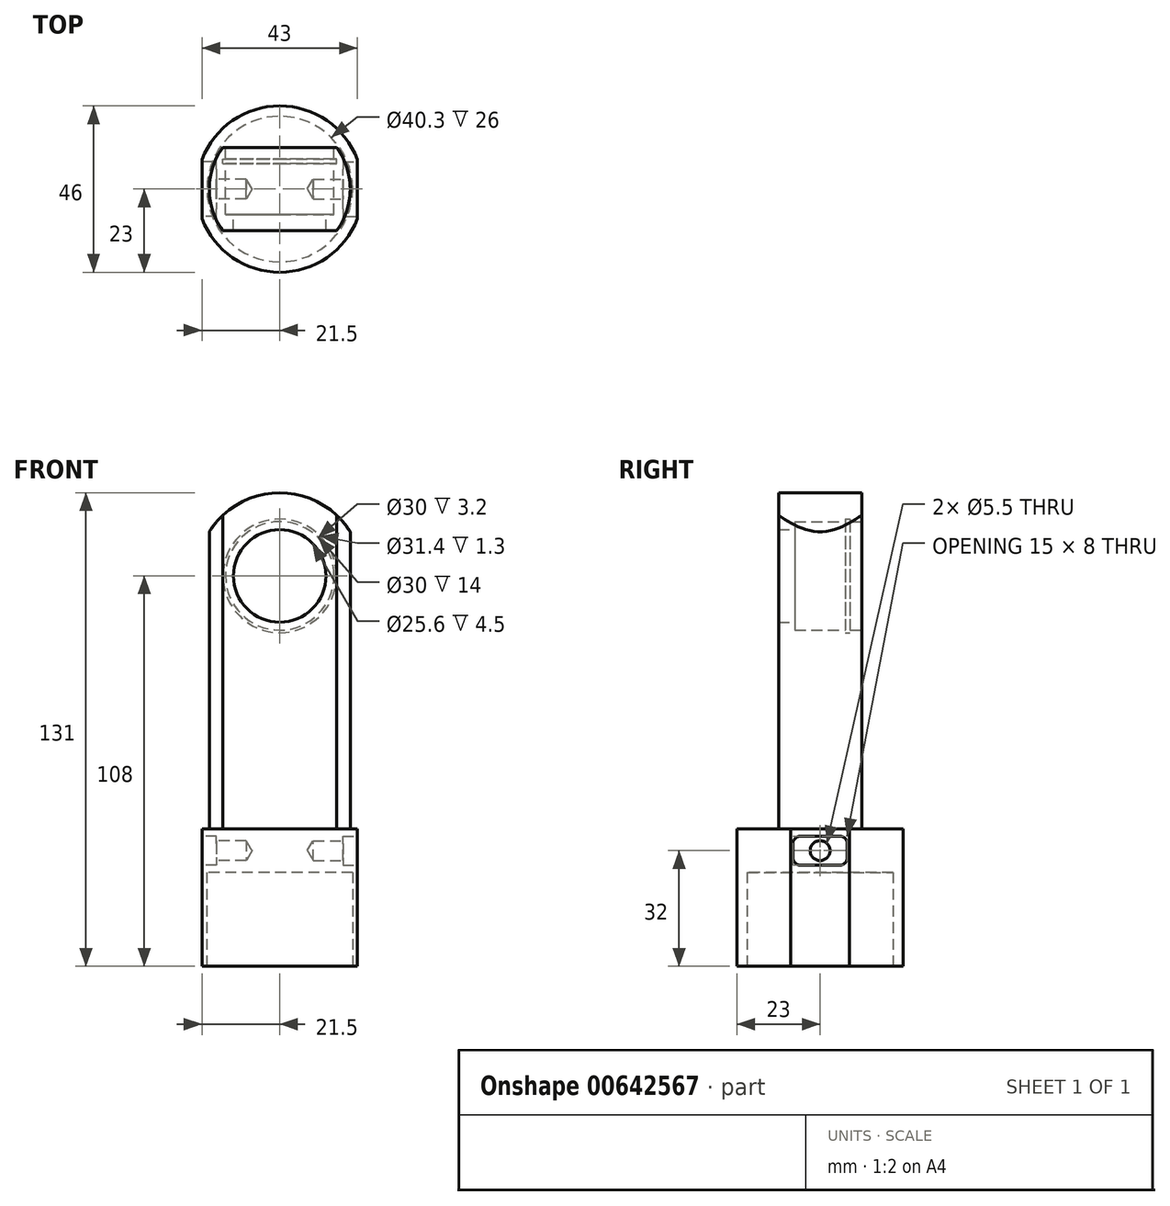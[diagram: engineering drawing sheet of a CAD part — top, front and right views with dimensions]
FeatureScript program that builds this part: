
annotation { "Feature Type Name" : "Feature", "Feature Type Description" : "" }
export const myFeature = defineFeature(function(context is Context, id is Id, definition is map)
    precondition{}
    {
        {
            var Q0;
            Q0=qCreatedBy(makeId("Top.planeOp"),FACE);
            var sketch = newSketch(context, id + "F0", { "sketchPlane" : qUnion([Q0])});
            skArc(sketch, "E0", {"start": v(-8.17, 21.5) * mm, "mid": v(-16.26, 16.26) * mm, "end": v(-21.5, 8.17) * mm});
            skArc(sketch, "E1.trimOffspring", {"start": v(8.17, -21.5) * mm, "mid": v(16.26, -16.26) * mm, "end": v(21.5, -8.17) * mm});
            skArc(sketch, "E2", {"start": v(-21.5, -8.17) * mm, "mid": v(0, -23) * mm, "end": v(21.5, -8.17) * mm});
            skLineSegment(sketch, "E3", {"start": v(-21.5, -8.17) * mm, "end": v(-21.5, 8.17) * mm});
            skLineSegment(sketch, "E4.MirrorCS", {"start": v(21.5, -8.17) * mm, "end": v(21.5, 8.17) * mm});
            skArc(sketch, "E5.trimOffspring", {"start": v(-21.5, -8.17) * mm, "mid": v(-16.26, -16.26) * mm, "end": v(-8.17, -21.5) * mm});
            skArc(sketch, "E6.trimOffspring", {"start": v(21.5, 8.17) * mm, "mid": v(0, 23) * mm, "end": v(-21.5, 8.17) * mm});
            skArc(sketch, "E7.trimOffspring", {"start": v(21.5, 8.17) * mm, "mid": v(16.26, 16.26) * mm, "end": v(8.17, 21.5) * mm});
            skSolve(sketch);
        }
        {
            var Q0;
            {var subQ2=sQuery(id+"F0.wireOp",EDGE,"E3");Q0=makeQuery(id+"F0.imprint","IMPRINT",FACE,{"disambiguationData":[TD([[makeQuery(id+"F0.imprint","IMPRINT",EDGE,{"derivedFrom":subQ2}),-1.0]])]});}
            extrude(context, id + "F1", {"entities" : qUnion([Q0]), "depth" : 38 * mm, "offsetDistance" : 25 * mm});
        }
        {
            var Q0;
            Q0=qCreatedBy(makeId("Top.planeOp"),FACE);
            var sketch = newSketch(context, id + "F2", { "sketchPlane" : qUnion([Q0])});
            skCircle(sketch, "E8", {"center": v(0, 0) * mm, "radius": 20.15 * mm});
            skSolve(sketch);
        }
        {
            var Q0;
            Q0=makeQuery(id+"F2.imprint","IMPRINT",FACE,{"disambiguationData":[TD([[makeQuery(id+"F2.imprint","IMPRINT",EDGE,{"derivedFrom":sQuery(id+"F2.wireOp",EDGE,"E8")}),1.0]])]});
            extrude(context, id + "F3", {"entities" : qUnion([Q0]), "operationType" : NewBodyOperationType.REMOVE, "depth" : 26 * mm, "offsetDistance" : 25 * mm});
        }
        {
            var Q0;
            Q0=makeQuery(id+"F1.opExtrude","CAP_FACE",FACE,{"disambiguationData":[OSD([sQuery(id+"F0.wireOp",EDGE,"E2"),sQuery(id+"F0.wireOp",EDGE,"E3"),sQuery(id+"F0.wireOp",EDGE,"E4.MirrorCS"),sQuery(id+"F0.wireOp",EDGE,"E5.trimOffspring"),sQuery(id+"F0.wireOp",EDGE,"E6.trimOffspring"),sQuery(id+"F0.wireOp",EDGE,"E7.trimOffspring")])],"isStart":false});
            var sketch = newSketch(context, id + "F4", { "sketchPlane" : qUnion([Q0])});
            skArc(sketch, "E9", {"start": v(-15.75, 11.5) * mm, "mid": v(-19.5, 0) * mm, "end": v(-15.75, -11.5) * mm});
            skLineSegment(sketch, "E10", {"start": v(-15.75, 11.5) * mm, "end": v(15.75, 11.5) * mm});
            skLineSegment(sketch, "E11.MirrorCS", {"start": v(-15.75, -11.5) * mm, "end": v(15.75, -11.5) * mm});
            skArc(sketch, "E12.trimOffspring", {"start": v(15.75, -11.5) * mm, "mid": v(19.5, 0) * mm, "end": v(15.75, 11.5) * mm});
            skSolve(sketch);
        }
        {
            var Q0;
            Q0=makeQuery(id+"F4.imprint","IMPRINT",FACE,{"disambiguationData":[TD([[makeQuery(id+"F4.imprint","IMPRINT",EDGE,{"derivedFrom":sQuery(id+"F4.wireOp",EDGE,"E9")}),1.0]])]});
            extrude(context, id + "F5", {"entities" : qUnion([Q0]), "operationType" : NewBodyOperationType.ADD, "depth" : 93 * mm, "offsetDistance" : 25 * mm});
        }
        {
            var Q0;
            Q0=qCreatedBy(makeId("Front.planeOp"),FACE);
            var sketch = newSketch(context, id + "F6", { "sketchPlane" : qUnion([Q0])});
            skArc(sketch, "E13", {"start": v(22.8, 111.07) * mm, "mid": v(-1.45, 130.95) * mm, "end": v(-23, 108.17) * mm});
            skLineSegment(sketch, "E14", {"start": v(-23, 108.17) * mm, "end": v(-36.61, 135.54) * mm});
            skLineSegment(sketch, "E15", {"start": v(-36.61, 135.54) * mm, "end": v(28.1, 135.54) * mm});
            skLineSegment(sketch, "E16", {"start": v(28.1, 135.54) * mm, "end": v(22.8, 111.07) * mm});
            skSolve(sketch);
        }
        {
            var Q0;
            Q0 = qSketchRegion(id + "F6", true);
            extrude(context, id + "F7", {"entities" : qUnion([Q0]), "operationType" : NewBodyOperationType.REMOVE, "oppositeDirection" : true, "depth" : 25 * mm, "offsetDistance" : 25 * mm, "symmetric" : true});
        }
        {
            var Q0;
            Q0=makeQuery(id+"F5.opExtrude","SWEPT_FACE",FACE,{"disambiguationData":[OSD([sQuery(id+"F4.wireOp",EDGE,"E10")])]});
            var sketch = newSketch(context, id + "F8", { "sketchPlane" : qUnion([Q0])});
            skCircle(sketch, "E17", {"center": v(0, 108) * mm, "radius": 15 * mm});
            skSolve(sketch);
        }
        {
            var Q0;
            Q0 = qSketchRegion(id + "F8", true);
            extrude(context, id + "F9", {"entities" : qUnion([Q0]), "operationType" : NewBodyOperationType.REMOVE, "oppositeDirection" : true, "depth" : 3.2 * mm, "offsetDistance" : 25 * mm});
        }
        {
            var Q0;
            Q0=makeQuery(id+"F9.boolean.opBoolean","COPY",FACE,{"derivedFrom":makeQuery(id+"F9.opExtrude","CAP_FACE",FACE,{"disambiguationData":[OSD([sQuery(id+"F8.wireOp",EDGE,"E17")])],"isStart":false})});
            var sketch = newSketch(context, id + "F10", { "sketchPlane" : qUnion([Q0])});
            skCircle(sketch, "E18", {"center": v(0, 108) * mm, "radius": 15.7 * mm});
            skSolve(sketch);
        }
        {
            var Q0;
            Q0 = qSketchRegion(id + "F10", true);
            extrude(context, id + "F11", {"entities" : qUnion([Q0]), "operationType" : NewBodyOperationType.REMOVE, "oppositeDirection" : true, "depth" : 1.3 * mm, "offsetDistance" : 25 * mm});
        }
        {
            var Q0;
            Q0=makeQuery(id+"F11.boolean.opBoolean","COPY",FACE,{"derivedFrom":makeQuery(id+"F11.opExtrude","CAP_FACE",FACE,{"disambiguationData":[OSD([sQuery(id+"F10.wireOp",EDGE,"E18")])],"isStart":false})});
            var sketch = newSketch(context, id + "F12", { "sketchPlane" : qUnion([Q0])});
            skCircle(sketch, "E19", {"center": v(0, 108) * mm, "radius": 15 * mm});
            skSolve(sketch);
        }
        {
            var Q0;
            Q0 = qSketchRegion(id + "F12", true);
            extrude(context, id + "F13", {"entities" : qUnion([Q0]), "operationType" : NewBodyOperationType.REMOVE, "oppositeDirection" : true, "depth" : 14 * mm, "offsetDistance" : 25 * mm});
        }
        {
            var Q0;
            Q0=makeQuery(id+"F13.boolean.opBoolean","COPY",FACE,{"derivedFrom":makeQuery(id+"F13.opExtrude","CAP_FACE",FACE,{"disambiguationData":[OSD([sQuery(id+"F12.wireOp",EDGE,"E19")])],"isStart":false})});
            var sketch = newSketch(context, id + "F14", { "sketchPlane" : qUnion([Q0])});
            skCircle(sketch, "E20", {"center": v(0, 108) * mm, "radius": 12.8 * mm});
            skSolve(sketch);
        }
        {
            var Q0;
            Q0 = qSketchRegion(id + "F14", true);
            extrude(context, id + "F15", {"entities" : qUnion([Q0]), "operationType" : NewBodyOperationType.REMOVE, "endBound" : BoundingType.THROUGH_ALL, "oppositeDirection" : true, "depth" : 25 * mm, "offsetDistance" : 25 * mm});
        }
        {
            var Q0;
            Q0=makeQuery(id+"F1.opExtrude","SWEPT_FACE",FACE,{"disambiguationData":[OSD([sQuery(id+"F0.wireOp",EDGE,"E4.MirrorCS")])]});
            var sketch = newSketch(context, id + "F16", { "sketchPlane" : qUnion([Q0])});
            skLineSegment(sketch, "E21.bottom", {"start": v(-5.5, 36) * mm, "end": v(5.5, 36) * mm});
            skLineSegment(sketch, "E21.top", {"start": v(-5.5, 28) * mm, "end": v(5.5, 28) * mm});
            skLineSegment(sketch, "E21.left", {"start": v(-7.5, 34) * mm, "end": v(-7.5, 30) * mm});
            skLineSegment(sketch, "E21.right", {"start": v(7.5, 34) * mm, "end": v(7.5, 30) * mm});
            skPoint(sketch, "E21.middle", {"position": v(0, 32) * mm});
            skPoint(sketch, "E22.visualSharp", {"position": v(-7.5, 36) * mm});
            skArc(sketch, "E22.filletArc", {"start": v(-5.5, 36) * mm, "mid": v(-6.91, 35.41) * mm, "end": v(-7.5, 34) * mm});
            skPoint(sketch, "E23.visualSharp", {"position": v(7.5, 36) * mm});
            skArc(sketch, "E23.filletArc", {"start": v(7.5, 34) * mm, "mid": v(6.91, 35.41) * mm, "end": v(5.5, 36) * mm});
            skPoint(sketch, "E24.visualSharp", {"position": v(7.5, 28) * mm});
            skArc(sketch, "E24.filletArc", {"start": v(5.5, 28) * mm, "mid": v(6.91, 28.59) * mm, "end": v(7.5, 30) * mm});
            skPoint(sketch, "E25.visualSharp", {"position": v(-7.5, 28) * mm});
            skArc(sketch, "E25.filletArc", {"start": v(-7.5, 30) * mm, "mid": v(-6.91, 28.59) * mm, "end": v(-5.5, 28) * mm});
            skSolve(sketch);
        }
        {
            var Q0;
            Q0 = qSketchRegion(id + "F16", true);
            extrude(context, id + "F17", {"entities" : qUnion([Q0]), "operationType" : NewBodyOperationType.REMOVE, "oppositeDirection" : true, "depth" : 4 * mm, "offsetDistance" : 25 * mm});
        }
        {
            var Q0;
            Q0=makeQuery(id+"F17.boolean.opBoolean","COPY",FACE,{"derivedFrom":makeQuery(id+"F17.opExtrude","CAP_FACE",FACE,{"disambiguationData":[OSD([sQuery(id+"F16.wireOp",EDGE,"E21.bottom"),sQuery(id+"F16.wireOp",EDGE,"E21.top"),sQuery(id+"F16.wireOp",EDGE,"E21.left"),sQuery(id+"F16.wireOp",EDGE,"E21.right"),sQuery(id+"F16.wireOp",EDGE,"E22.filletArc"),sQuery(id+"F16.wireOp",EDGE,"E23.filletArc"),sQuery(id+"F16.wireOp",EDGE,"E24.filletArc"),sQuery(id+"F16.wireOp",EDGE,"E25.filletArc")])],"isStart":false})});
            var sketch = newSketch(context, id + "F18", { "sketchPlane" : qUnion([Q0])});
            skPoint(sketch, "E26", {"position": v(0, 32) * mm});
            skSolve(sketch);
        }
        {
            var Q0;
            Q0=sQuery(id+"F18.wireOp",VERTEX,"E26");
            var Q1;
            Q1=makeQuery(id+"F1.opExtrude","SWEPT_BODY",BODY,{"disambiguationData":[OSD([sQuery(id+"F0.wireOp",EDGE,"E2"),sQuery(id+"F0.wireOp",EDGE,"E3"),sQuery(id+"F0.wireOp",EDGE,"E4.MirrorCS"),sQuery(id+"F0.wireOp",EDGE,"E5.trimOffspring"),sQuery(id+"F0.wireOp",EDGE,"E6.trimOffspring"),sQuery(id+"F0.wireOp",EDGE,"E7.trimOffspring")])]});
            hole(context, id + "F19", {"style" : HoleStyle.SIMPLE, "endStyle" : HoleEndStyle.BLIND, "holeDiameter" : 5.5 * mm, "majorDiameter" : 5 * mm, "holeDepth" : 8.2 * mm, "isTappedThrough" : true, "tappedDepth" : 12 * mm, "tapClearance" : 3, "locations" : qUnion([Q0]), "scope" : qUnion([Q1])});
        }
        {
            var Q0;
            Q0=makeQuery(id+"F1.opExtrude","SWEPT_FACE",FACE,{"disambiguationData":[OSD([sQuery(id+"F0.wireOp",EDGE,"E3")])]});
            var sketch = newSketch(context, id + "F20", { "sketchPlane" : qUnion([Q0])});
            skLineSegment(sketch, "E27.bottom", {"start": v(-5.5, 36) * mm, "end": v(5.5, 36) * mm});
            skLineSegment(sketch, "E27.top", {"start": v(-5.5, 28) * mm, "end": v(5.5, 28) * mm});
            skLineSegment(sketch, "E27.left", {"start": v(-7.5, 34) * mm, "end": v(-7.5, 30) * mm});
            skLineSegment(sketch, "E27.right", {"start": v(7.5, 34) * mm, "end": v(7.5, 30) * mm});
            skPoint(sketch, "E27.middle", {"position": v(0, 32) * mm});
            skPoint(sketch, "E28.visualSharp", {"position": v(-7.5, 36) * mm});
            skArc(sketch, "E28.filletArc", {"start": v(-5.5, 36) * mm, "mid": v(-6.91, 35.41) * mm, "end": v(-7.5, 34) * mm});
            skPoint(sketch, "E29.visualSharp", {"position": v(7.5, 36) * mm});
            skArc(sketch, "E29.filletArc", {"start": v(7.5, 34) * mm, "mid": v(6.91, 35.41) * mm, "end": v(5.5, 36) * mm});
            skPoint(sketch, "E30.visualSharp", {"position": v(7.5, 28) * mm});
            skArc(sketch, "E30.filletArc", {"start": v(5.5, 28) * mm, "mid": v(6.91, 28.59) * mm, "end": v(7.5, 30) * mm});
            skPoint(sketch, "E31.visualSharp", {"position": v(-7.5, 28) * mm});
            skArc(sketch, "E31.filletArc", {"start": v(-7.5, 30) * mm, "mid": v(-6.91, 28.59) * mm, "end": v(-5.5, 28) * mm});
            skSolve(sketch);
        }
        {
            var Q0;
            Q0 = qSketchRegion(id + "F20", true);
            extrude(context, id + "F21", {"entities" : qUnion([Q0]), "operationType" : NewBodyOperationType.REMOVE, "oppositeDirection" : true, "depth" : 4 * mm, "offsetDistance" : 25 * mm});
        }
        {
            var Q0;
            Q0=makeQuery(id+"F21.boolean.opBoolean","COPY",FACE,{"derivedFrom":makeQuery(id+"F21.opExtrude","CAP_FACE",FACE,{"disambiguationData":[OSD([sQuery(id+"F20.wireOp",EDGE,"E27.bottom"),sQuery(id+"F20.wireOp",EDGE,"E27.top"),sQuery(id+"F20.wireOp",EDGE,"E27.left"),sQuery(id+"F20.wireOp",EDGE,"E27.right"),sQuery(id+"F20.wireOp",EDGE,"E28.filletArc"),sQuery(id+"F20.wireOp",EDGE,"E29.filletArc"),sQuery(id+"F20.wireOp",EDGE,"E30.filletArc"),sQuery(id+"F20.wireOp",EDGE,"E31.filletArc")])],"isStart":false})});
            var sketch = newSketch(context, id + "F22", { "sketchPlane" : qUnion([Q0])});
            skPoint(sketch, "E32", {"position": v(0, 32) * mm});
            skSolve(sketch);
        }
        {
            var Q0;
            Q0=sQuery(id+"F22.wireOp",VERTEX,"E32");
            var Q1;
            Q1=makeQuery(id+"F1.opExtrude","SWEPT_BODY",BODY,{"disambiguationData":[OSD([sQuery(id+"F0.wireOp",EDGE,"E2"),sQuery(id+"F0.wireOp",EDGE,"E3"),sQuery(id+"F0.wireOp",EDGE,"E4.MirrorCS"),sQuery(id+"F0.wireOp",EDGE,"E5.trimOffspring"),sQuery(id+"F0.wireOp",EDGE,"E6.trimOffspring"),sQuery(id+"F0.wireOp",EDGE,"E7.trimOffspring")])]});
            hole(context, id + "F23", {"style" : HoleStyle.SIMPLE, "endStyle" : HoleEndStyle.BLIND, "holeDiameter" : 5.5 * mm, "majorDiameter" : 5 * mm, "holeDepth" : 8.2 * mm, "isTappedThrough" : true, "tappedDepth" : 12 * mm, "tapClearance" : 3, "locations" : qUnion([Q0]), "scope" : qUnion([Q1])});
        }
    });
